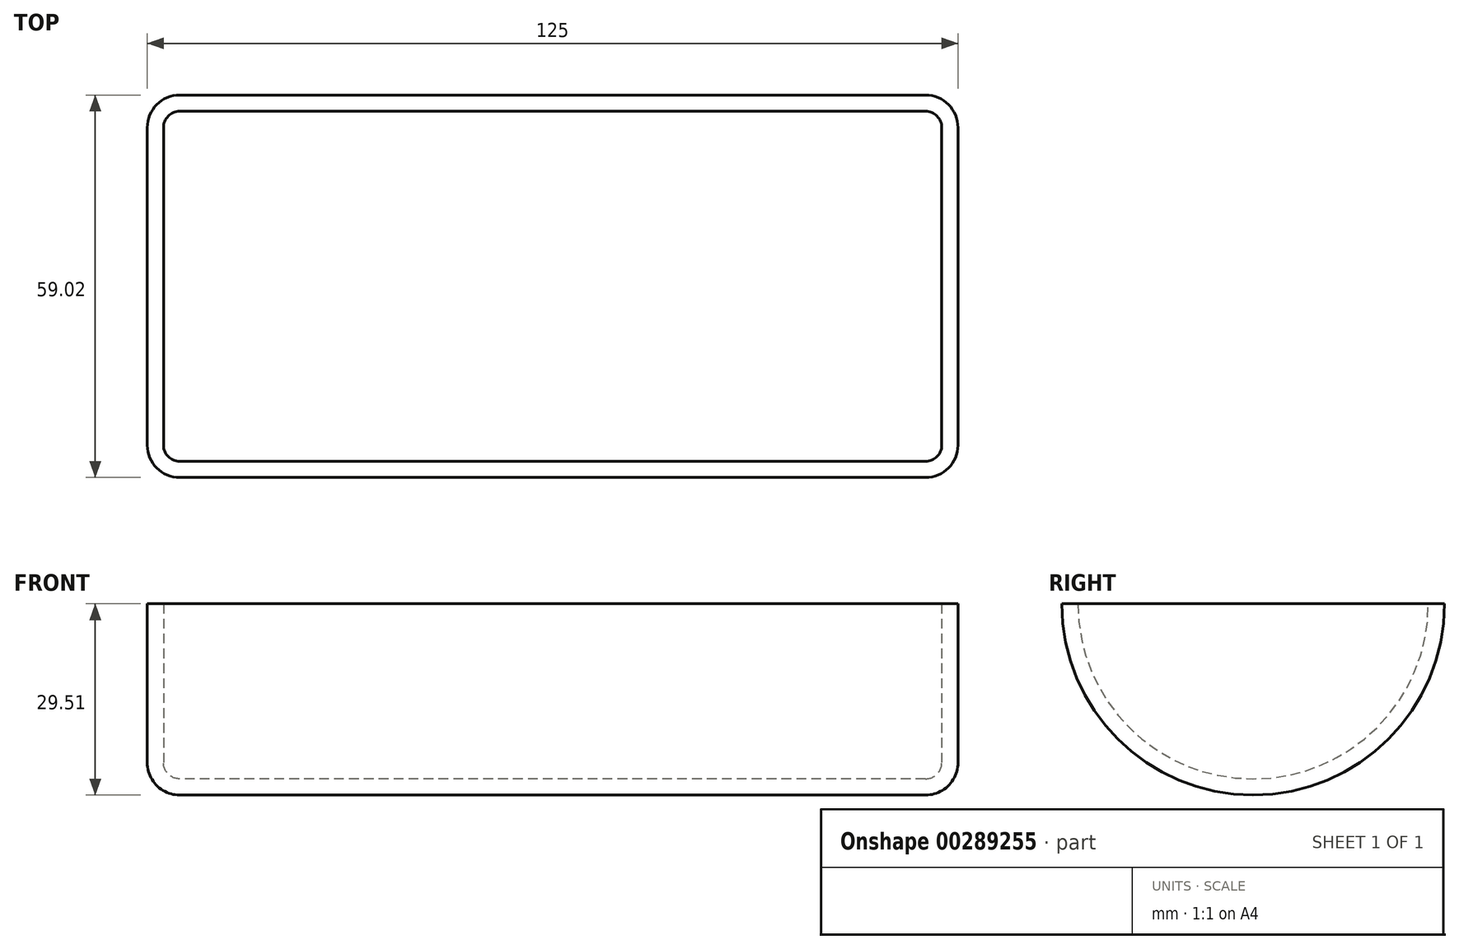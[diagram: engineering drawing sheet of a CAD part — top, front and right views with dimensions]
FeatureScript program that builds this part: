
annotation { "Feature Type Name" : "Feature", "Feature Type Description" : "" }
export const myFeature = defineFeature(function(context is Context, id is Id, definition is map)
    precondition{}
    {
        {
            var Q0;
            Q0=qCreatedBy(makeId("Right.planeOp"),FACE);
            var sketch = newSketch(context, id + "F0", { "sketchPlane" : qUnion([Q0])});
            skCircle(sketch, "E0", {"center": v(0, 0) * mm, "radius": 29.51 * mm});
            skSolve(sketch);
        }
        {
            var Q0;
            Q0 = qSketchRegion(id + "F0", true);
            extrude(context, id + "F1", {"entities" : qUnion([Q0]), "depth" : 125 * mm});
        }
        {
            var Q0;
            Q0=makeQuery(id+"F1.opExtrude","CAP_EDGE",EDGE,{"disambiguationData":[OSD([sQuery(id+"F0.wireOp",EDGE,"E0")])],"isStart":true});
            var Q1;
            Q1=makeQuery(id+"F1.opExtrude","CAP_EDGE",EDGE,{"disambiguationData":[OSD([sQuery(id+"F0.wireOp",EDGE,"E0")])],"isStart":false});
            fillet(context, id + "F2", {"entities" : qUnion([Q0, Q1]), "radius" : 5 * mm, "tangentPropagation" : true, "allowEdgeOverflow" : false});
        }
        {
            var Q0;
            Q0=qCreatedBy(makeId("Top.planeOp"),FACE);
            var sketch = newSketch(context, id + "F3", { "sketchPlane" : qUnion([Q0])});
            skLineSegment(sketch, "E1.bottom", {"start": v(159.06, -48.17) * mm, "end": v(-214.82, -48.17) * mm});
            skLineSegment(sketch, "E1.top", {"start": v(159.06, 131.34) * mm, "end": v(-214.82, 131.34) * mm});
            skLineSegment(sketch, "E1.left", {"start": v(159.06, -48.17) * mm, "end": v(159.06, 131.34) * mm});
            skLineSegment(sketch, "E1.right", {"start": v(-214.82, -48.17) * mm, "end": v(-214.82, 131.34) * mm});
            skPoint(sketch, "E1.middle", {"position": v(-27.88, 41.59) * mm});
            skSolve(sketch);
        }
        {
            var Q0;
            Q0 = qSketchRegion(id + "F3", true);
            extrude(context, id + "F4", {"entities" : qUnion([Q0]), "operationType" : NewBodyOperationType.REMOVE, "endBound" : BoundingType.THROUGH_ALL, "depth" : 25 * mm});
        }
        {
            var Q0;
            Q0=makeQuery(id+"F4.boolean.opBoolean","COPY",FACE,{"derivedFrom":makeQuery(id+"F4.opExtrude","CAP_FACE",FACE,{"disambiguationData":[OSD([sQuery(id+"F3.wireOp",EDGE,"E1.bottom"),sQuery(id+"F3.wireOp",EDGE,"E1.top"),sQuery(id+"F3.wireOp",EDGE,"E1.left"),sQuery(id+"F3.wireOp",EDGE,"E1.right")])],"isStart":true})});
            shell(context, id + "F5", {"entities" : qUnion([Q0]), "thickness" : 2.5 * mm});
        }
    });
